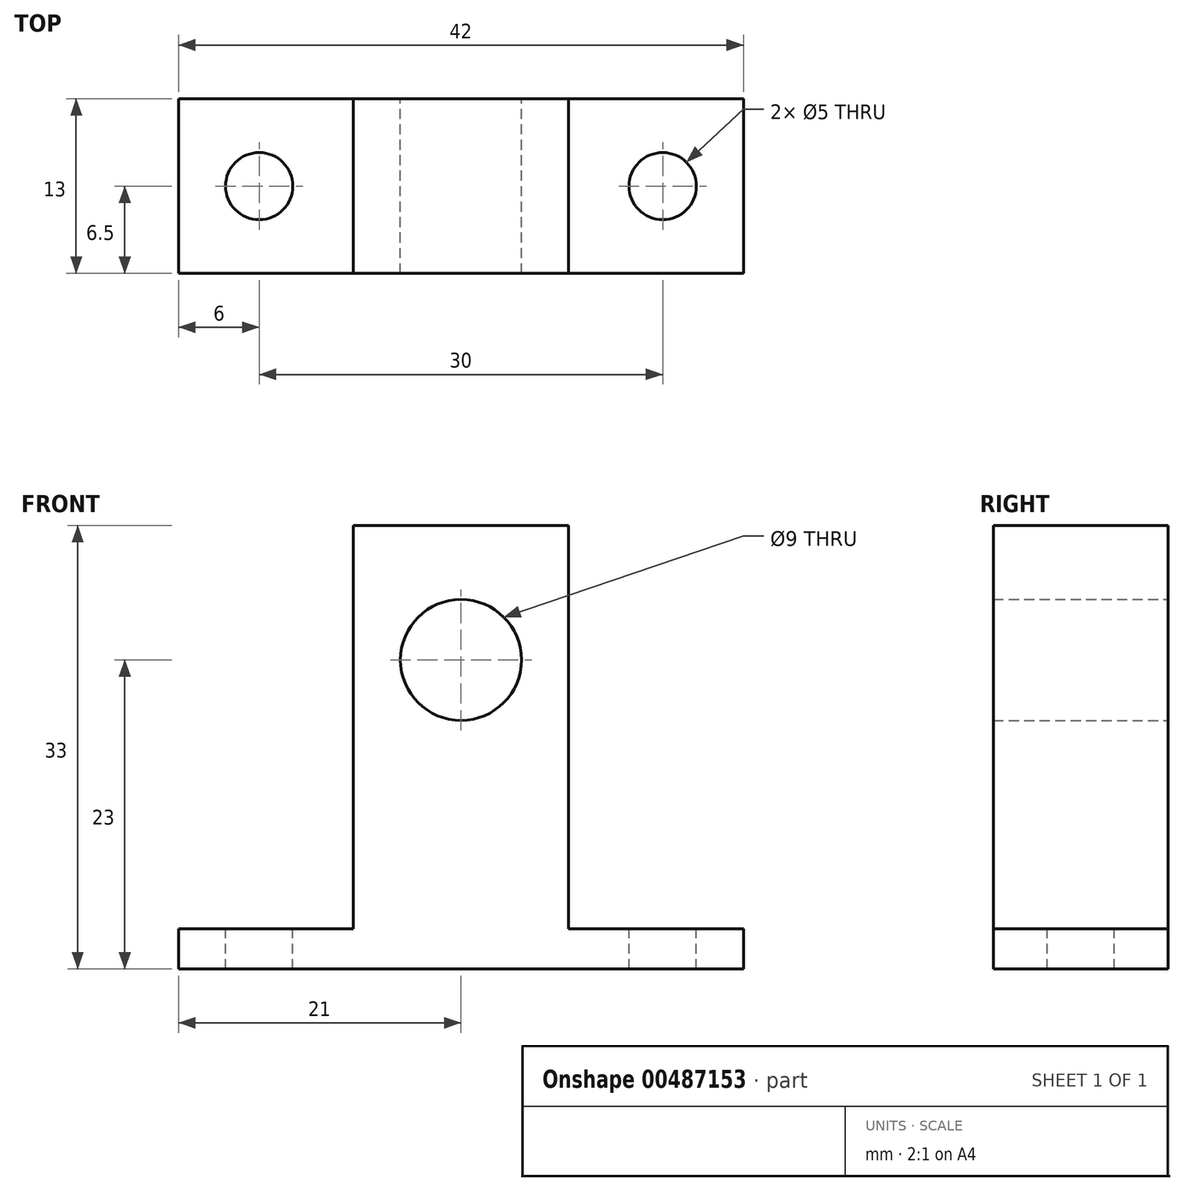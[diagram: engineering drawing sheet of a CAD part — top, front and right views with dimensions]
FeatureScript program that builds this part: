
annotation { "Feature Type Name" : "Feature", "Feature Type Description" : "" }
export const myFeature = defineFeature(function(context is Context, id is Id, definition is map)
    precondition{}
    {
        {
            var Q0;
            Q0=qCreatedBy(makeId("Front.planeOp"),FACE);
            var sketch = newSketch(context, id + "F0", { "sketchPlane" : qUnion([Q0])});
            skCircle(sketch, "E0", {"center": v(0, 0) * mm, "radius": 4.5 * mm});
            skLineSegment(sketch, "E1.bottom", {"start": v(-8, 10) * mm, "end": v(8, 10) * mm});
            skLineSegment(sketch, "E1.top", {"start": v(-8, -23) * mm, "end": v(8, -23) * mm});
            skLineSegment(sketch, "E1.left", {"start": v(-8, 10) * mm, "end": v(-8, -20) * mm});
            skLineSegment(sketch, "E1.right", {"start": v(8, 10) * mm, "end": v(8, -20) * mm});
            skLineSegment(sketch, "E2.bottom", {"start": v(-21, -23) * mm, "end": v(-8, -23) * mm});
            skLineSegment(sketch, "E2.top", {"start": v(-21, -20) * mm, "end": v(-8, -20) * mm});
            skLineSegment(sketch, "E2.left", {"start": v(-21, -23) * mm, "end": v(-21, -20) * mm});
            skLineSegment(sketch, "E2.right", {"start": v(21, -23) * mm, "end": v(21, -20) * mm});
            skLineSegment(sketch, "E3.trimOffspring", {"start": v(8, -20) * mm, "end": v(21, -20) * mm});
            skLineSegment(sketch, "E4.trimOffspring", {"start": v(8, -23) * mm, "end": v(21, -23) * mm});
            skSolve(sketch);
        }
        {
            var Q0;
            Q0 = qSketchRegion(id + "F0", true);
            extrude(context, id + "F1", {"entities" : qUnion([Q0]), "depth" : 13 * mm});
        }
        {
            var Q0;
            Q0=makeQuery(id+"F1.opExtrude","SWEPT_FACE",FACE,{"disambiguationData":[OSD([sQuery(id+"F0.wireOp",EDGE,"E3.trimOffspring")])]});
            var sketch = newSketch(context, id + "F2", { "sketchPlane" : qUnion([Q0])});
            skCircle(sketch, "E5", {"center": v(15, -6.5) * mm, "radius": 2.5 * mm});
            skCircle(sketch, "E6", {"center": v(-15, -6.5) * mm, "radius": 2.5 * mm});
            skSolve(sketch);
        }
        {
            var Q0;
            Q0 = qSketchRegion(id + "F2", true);
            extrude(context, id + "F3", {"entities" : qUnion([Q0]), "operationType" : NewBodyOperationType.REMOVE, "oppositeDirection" : true, "depth" : 25 * mm});
        }
    });
